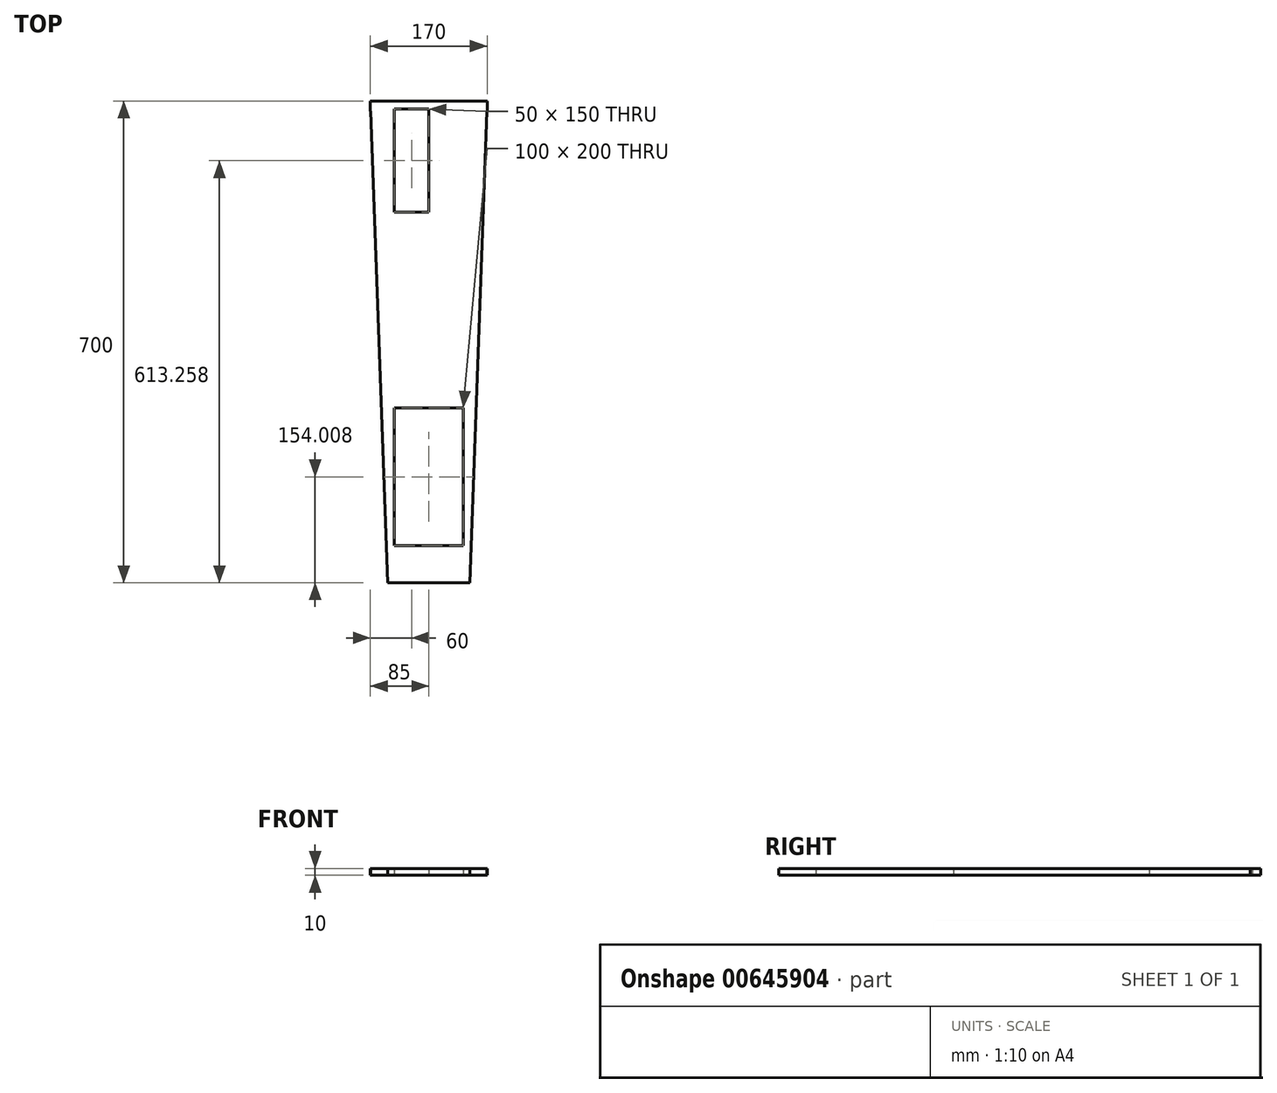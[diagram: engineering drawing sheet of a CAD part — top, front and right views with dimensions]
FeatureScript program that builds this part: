
annotation { "Feature Type Name" : "Feature", "Feature Type Description" : "" }
export const myFeature = defineFeature(function(context is Context, id is Id, definition is map)
    precondition{}
    {
        {
            var Q0;
            Q0=qCreatedBy(makeId("Top.planeOp"),FACE);
            var sketch = newSketch(context, id + "F0", { "sketchPlane" : qUnion([Q0])});
            skLineSegment(sketch, "E0.bottom", {"start": v(85, -7.5) * mm, "end": v(-85, -7.5) * mm});
            skLineSegment(sketch, "E0.top", {"start": v(85, 7.5) * mm, "end": v(-85, 7.5) * mm});
            skLineSegment(sketch, "E0.left", {"start": v(85, -7.5) * mm, "end": v(85, 7.5) * mm});
            skLineSegment(sketch, "E0.right", {"start": v(-85, -7.5) * mm, "end": v(-85, 7.5) * mm});
            skPoint(sketch, "E0.middle", {"position": v(0, 0) * mm});
            skLineSegment(sketch, "E1.bottom", {"start": v(60, -670.57) * mm, "end": v(-60, -670.57) * mm});
            skLineSegment(sketch, "E1.top", {"start": v(60, -692.5) * mm, "end": v(-60, -692.5) * mm});
            skLineSegment(sketch, "E1.left", {"start": v(60, -670.57) * mm, "end": v(60, -692.5) * mm});
            skLineSegment(sketch, "E1.right", {"start": v(-60, -670.57) * mm, "end": v(-60, -692.5) * mm});
            skPoint(sketch, "E1.middle", {"position": v(0, -681.54) * mm});
            skLineSegment(sketch, "E2", {"start": v(85, 7.5) * mm, "end": v(60, -692.5) * mm});
            skLineSegment(sketch, "E3", {"start": v(-85, 7.5) * mm, "end": v(-60, -692.5) * mm});
            skLineSegment(sketch, "E4.bottom", {"start": v(50, -438.5) * mm, "end": v(-50, -438.5) * mm});
            skLineSegment(sketch, "E4.top", {"start": v(50, -638.5) * mm, "end": v(-50, -638.5) * mm});
            skLineSegment(sketch, "E4.left", {"start": v(50, -438.5) * mm, "end": v(50, -638.5) * mm});
            skLineSegment(sketch, "E4.right", {"start": v(-50, -438.5) * mm, "end": v(-50, -638.5) * mm});
            skPoint(sketch, "E4.middle", {"position": v(0, -538.5) * mm});
            skPoint(sketch, "E5.firstSnap0", {"position": v(0, -7.5) * mm});
            skLineSegment(sketch, "E5.bottom", {"start": v(0, -4.24) * mm, "end": v(-50, -4.24) * mm});
            skLineSegment(sketch, "E5.top", {"start": v(0, -154.24) * mm, "end": v(-50, -154.24) * mm});
            skLineSegment(sketch, "E5.left", {"start": v(0, -4.24) * mm, "end": v(0, -154.24) * mm});
            skLineSegment(sketch, "E5.right", {"start": v(-50, -4.24) * mm, "end": v(-50, -154.24) * mm});
            skSolve(sketch);
        }
        {
            var Q0;
            Q0 = qSketchRegion(id + "F0", true);
            extrude(context, id + "F1", {"entities" : qUnion([Q0]), "depth" : 10 * mm, "offsetDistance" : 25 * mm});
        }
    });
